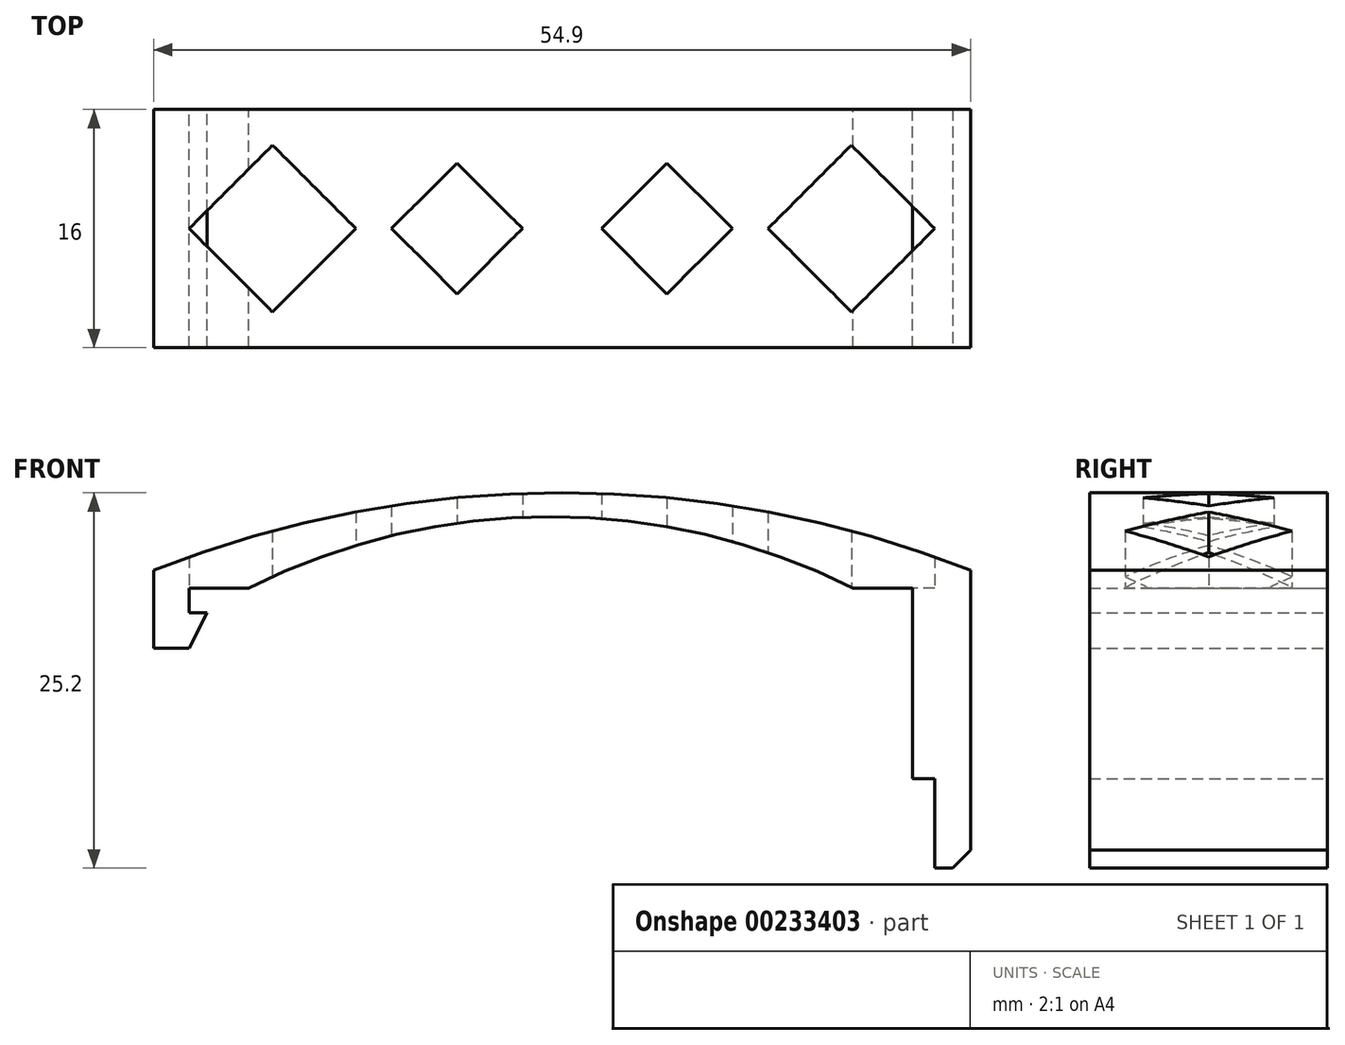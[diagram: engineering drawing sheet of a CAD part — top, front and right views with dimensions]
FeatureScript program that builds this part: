
annotation { "Feature Type Name" : "Feature", "Feature Type Description" : "" }
export const myFeature = defineFeature(function(context is Context, id is Id, definition is map)
    precondition{}
    {
        {
            var Q0;
            Q0=qCreatedBy(makeId("Front.planeOp"),FACE);
            var sketch = newSketch(context, id + "F0", { "sketchPlane" : qUnion([Q0])});
            skLineSegment(sketch, "E0", {"start": v(0, 0) * mm, "end": v(48.6, 0) * mm, "construction": true});
            skLineSegment(sketch, "E1", {"start": v(48.6, 0) * mm, "end": v(48.6, -13.2) * mm, "construction": true});
            skLineSegment(sketch, "E2", {"start": v(48.6, -13.2) * mm, "end": v(47.2, -13.2) * mm, "construction": true});
            skLineSegment(sketch, "E3", {"start": v(47.2, -13.2) * mm, "end": v(47.2, -1.4) * mm, "construction": true});
            skLineSegment(sketch, "E4", {"start": v(47.2, -1.4) * mm, "end": v(0, -1.4) * mm, "construction": true});
            skLineSegment(sketch, "E5", {"start": v(0, -1.4) * mm, "end": v(0, 0) * mm, "construction": true});
            skSolve(sketch);
        }
        {
            var Q0;
            Q0=qCreatedBy(makeId("Front.planeOp"),FACE);
            var sketch = newSketch(context, id + "F1", { "sketchPlane" : qUnion([Q0])});
            skLineSegment(sketch, "E6", {"start": v(0, -4.05) * mm, "end": v(-2.4, -4.05) * mm});
            skLineSegment(sketch, "E7", {"start": v(-2.4, -4.05) * mm, "end": v(-2.4, 1.2) * mm});
            skLineSegment(sketch, "E8", {"start": v(0, 0) * mm, "end": v(4, 0) * mm});
            skLineSegment(sketch, "E9", {"start": v(44.6, 0) * mm, "end": v(48.6, 0) * mm});
            skLineSegment(sketch, "E10", {"start": v(48.6, 0) * mm, "end": v(48.6, -12.8) * mm});
            skLineSegment(sketch, "E11", {"start": v(52.5, -18.8) * mm, "end": v(52.5, 1.2) * mm});
            skArc(sketch, "E12", {"start": v(44.6, 0) * mm, "mid": v(24.3, 4.8) * mm, "end": v(4, 0) * mm});
            skArc(sketch, "E13", {"start": v(52.5, 1.2) * mm, "mid": v(25.05, 6.4) * mm, "end": v(-2.4, 1.2) * mm});
            skPoint(sketch, "E14", {"position": v(25.05, 6.4) * mm});
            skPoint(sketch, "E15", {"position": v(24.3, 4.8) * mm});
            skLineSegment(sketch, "E16", {"start": v(48.6, -12.8) * mm, "end": v(50.1, -12.8) * mm});
            skLineSegment(sketch, "E17", {"start": v(50.1, -12.8) * mm, "end": v(50.1, -18.8) * mm});
            skLineSegment(sketch, "E18", {"start": v(50.1, -18.8) * mm, "end": v(52.5, -18.8) * mm});
            skLineSegment(sketch, "E19", {"start": v(0, 0) * mm, "end": v(0, -1.65) * mm});
            skLineSegment(sketch, "E20", {"start": v(0, -1.65) * mm, "end": v(1.2, -1.65) * mm});
            skLineSegment(sketch, "E21", {"start": v(1.2, -1.65) * mm, "end": v(0, -4.05) * mm});
            skSolve(sketch);
        }
        {
            var Q0;
            Q0 = qSketchRegion(id + "F1", true);
            extrude(context, id + "F2", {"entities" : qUnion([Q0]), "endBound" : BoundingType.SYMMETRIC, "depth" : 16 * mm});
        }
        {
            var Q0;
            Q0=qCreatedBy(makeId("Top.planeOp"),FACE);
            var sketch = newSketch(context, id + "F3", { "sketchPlane" : qUnion([Q0])});
            skLineSegment(sketch, "E22", {"start": v(0, 0) * mm, "end": v(5.6, 5.6) * mm});
            skLineSegment(sketch, "E23", {"start": v(5.6, 5.6) * mm, "end": v(11.2, 0) * mm});
            skLineSegment(sketch, "E24", {"start": v(11.2, 0) * mm, "end": v(5.6, -5.6) * mm});
            skLineSegment(sketch, "E25", {"start": v(5.6, -5.6) * mm, "end": v(0, 0) * mm});
            skLineSegment(sketch, "E26", {"start": v(38.9, 0) * mm, "end": v(44.5, 5.6) * mm});
            skLineSegment(sketch, "E27", {"start": v(44.5, 5.6) * mm, "end": v(50.1, 0) * mm});
            skLineSegment(sketch, "E28", {"start": v(50.1, 0) * mm, "end": v(44.5, -5.6) * mm});
            skLineSegment(sketch, "E29", {"start": v(44.5, -5.6) * mm, "end": v(38.9, 0) * mm});
            skLineSegment(sketch, "E30", {"start": v(32.1, 4.4) * mm, "end": v(27.7, 0) * mm});
            skLineSegment(sketch, "E31", {"start": v(27.7, 0) * mm, "end": v(32.1, -4.4) * mm});
            skLineSegment(sketch, "E32", {"start": v(32.1, -4.4) * mm, "end": v(36.5, 0) * mm});
            skLineSegment(sketch, "E33", {"start": v(36.5, 0) * mm, "end": v(32.1, 4.4) * mm});
            skLineSegment(sketch, "E34", {"start": v(18, 4.4) * mm, "end": v(13.6, 0) * mm});
            skLineSegment(sketch, "E35", {"start": v(13.6, 0) * mm, "end": v(18, -4.4) * mm});
            skLineSegment(sketch, "E36", {"start": v(18, -4.4) * mm, "end": v(22.4, 0) * mm});
            skLineSegment(sketch, "E37", {"start": v(22.4, 0) * mm, "end": v(18, 4.4) * mm});
            skSolve(sketch);
        }
        {
            var Q0;
            Q0 = qSketchRegion(id + "F3", true);
            extrude(context, id + "F4", {"entities" : qUnion([Q0]), "operationType" : NewBodyOperationType.REMOVE, "endBound" : BoundingType.THROUGH_ALL, "depth" : 25 * mm});
        }
        {
            var Q0;
            Q0=makeQuery(id+"F2.opExtrude","SWEPT_EDGE",EDGE,{"disambiguationData":[OSD([sQuery(id+"F1.wireOp",EDGE,"E11"),sQuery(id+"F1.wireOp",EDGE,"E18")])]});
            chamfer(context, id + "F5", {"entities" : qUnion([Q0]), "width" : 1.2 * mm, "tangentPropagation" : true});
        }
    });
